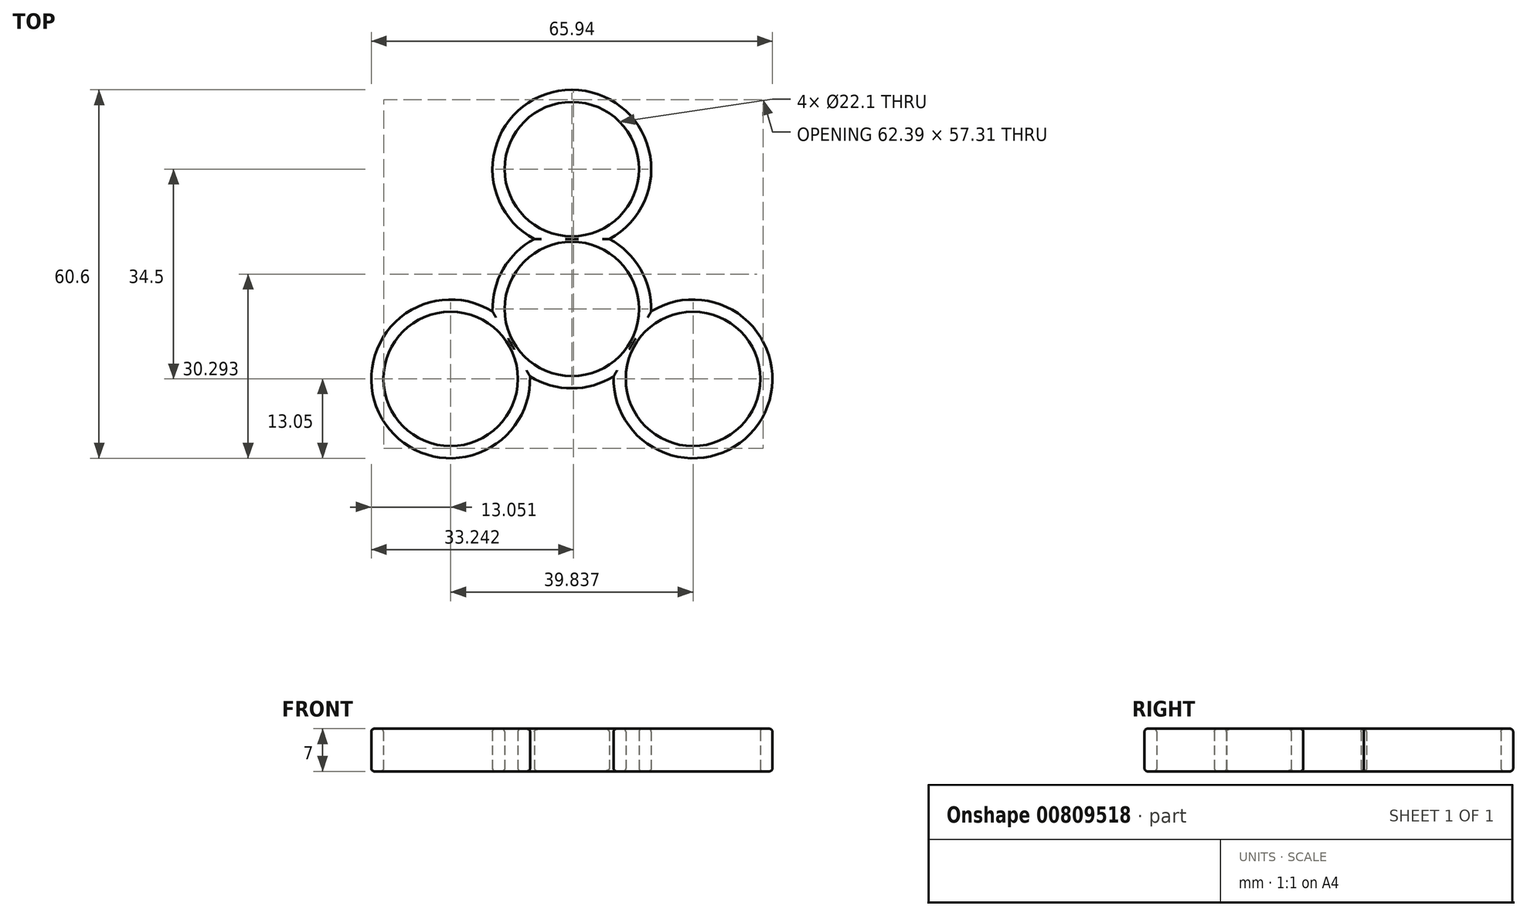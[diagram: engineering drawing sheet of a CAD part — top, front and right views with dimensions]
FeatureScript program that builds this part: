
annotation { "Feature Type Name" : "Feature", "Feature Type Description" : "" }
export const myFeature = defineFeature(function(context is Context, id is Id, definition is map)
    precondition{}
    {
        {
            var Q0;
            Q0=qCreatedBy(makeId("Top.planeOp"),FACE);
            var sketch = newSketch(context, id + "F0", { "sketchPlane" : qUnion([Q0])});
            skCircle(sketch, "E0", {"center": v(0, 0) * mm, "radius": 11.05 * mm});
            skCircle(sketch, "E1", {"center": v(0, 23) * mm, "radius": 11.05 * mm});
            skCircle(sketch, "E2", {"center": v(0, 23) * mm, "radius": 13.05 * mm});
            skCircle(sketch, "E3", {"center": v(0, 0) * mm, "radius": 13.05 * mm});
            skCircle(sketch, "E4.1.0", {"center": v(-19.92, -11.5) * mm, "radius": 11.05 * mm});
            skCircle(sketch, "E4.1.1", {"center": v(-19.92, -11.5) * mm, "radius": 13.05 * mm});
            skCircle(sketch, "E4.2.0", {"center": v(19.92, -11.5) * mm, "radius": 11.05 * mm});
            skCircle(sketch, "E4.2.1", {"center": v(19.92, -11.5) * mm, "radius": 13.05 * mm});
            skSolve(sketch);
        }
        {
            var Q0;
            {var subQ0=sQuery(id+"F0.wireOp",EDGE,"E3");var subQ1=sQuery(id+"F0.wireOp",EDGE,"E1");var subQ2=makeQuery(id+"F0.imprint","INTERSECT",VERTEX,{"disambiguationData":[OD(0.0)],"derivedFrom":[subQ1,subQ0]});Q0=makeQuery(id+"F0.imprint","IMPRINT",FACE,{"disambiguationData":[TD([[makeQuery(id+"F0.imprint","IMPRINT",EDGE,{"disambiguationData":[TD([[subQ2,1.0]])],"derivedFrom":subQ1}),-1.0]])]});}
            var Q1;
            {var subQ0=sQuery(id+"F0.wireOp",EDGE,"E1");var subQ1=sQuery(id+"F0.wireOp",EDGE,"E0");var subQ2=makeQuery(id+"F0.imprint","INTERSECT",VERTEX,{"derivedFrom":[subQ1,subQ0]});Q1=makeQuery(id+"F0.imprint","IMPRINT",FACE,{"disambiguationData":[TD([[makeQuery(id+"F0.imprint","IMPRINT",EDGE,{"disambiguationData":[TD([[subQ2,-1.0]])],"derivedFrom":subQ1}),-1.0]])]});}
            var Q2;
            {var subQ0=sQuery(id+"F0.wireOp",EDGE,"E2");var subQ1=sQuery(id+"F0.wireOp",EDGE,"E0");var subQ2=makeQuery(id+"F0.imprint","INTERSECT",VERTEX,{"disambiguationData":[OD(0.0)],"derivedFrom":[subQ1,subQ0]});Q2=makeQuery(id+"F0.imprint","IMPRINT",FACE,{"disambiguationData":[TD([[makeQuery(id+"F0.imprint","IMPRINT",EDGE,{"disambiguationData":[TD([[subQ2,1.0]])],"derivedFrom":subQ1}),-1.0]])]});}
            var Q3;
            {var subQ0=sQuery(id+"F0.wireOp",EDGE,"E1");var subQ1=sQuery(id+"F0.wireOp",EDGE,"E0");var subQ2=makeQuery(id+"F0.imprint","INTERSECT",VERTEX,{"derivedFrom":[subQ1,subQ0]});Q3=makeQuery(id+"F0.imprint","IMPRINT",FACE,{"disambiguationData":[TD([[makeQuery(id+"F0.imprint","IMPRINT",EDGE,{"disambiguationData":[TD([[subQ2,1.0]])],"derivedFrom":subQ1}),-1.0]])]});}
            var Q4;
            {var subQ0=sQuery(id+"F0.wireOp",EDGE,"E3");var subQ1=sQuery(id+"F0.wireOp",EDGE,"E1");var subQ2=makeQuery(id+"F0.imprint","INTERSECT",VERTEX,{"disambiguationData":[OD(0.0)],"derivedFrom":[subQ1,subQ0]});Q4=makeQuery(id+"F0.imprint","IMPRINT",FACE,{"disambiguationData":[TD([[makeQuery(id+"F0.imprint","IMPRINT",EDGE,{"disambiguationData":[TD([[subQ2,-1.0]])],"derivedFrom":subQ1}),-1.0]])]});}
            var Q5;
            {var subQ4=sQuery(id+"F0.wireOp",EDGE,"E4.1.1");var subQ5=sQuery(id+"F0.wireOp",EDGE,"E0");var subQ6=makeQuery(id+"F0.imprint","INTERSECT",VERTEX,{"disambiguationData":[OD(0.0)],"derivedFrom":[subQ5,subQ4]});Q5=makeQuery(id+"F0.imprint","IMPRINT",FACE,{"disambiguationData":[TD([[makeQuery(id+"F0.imprint","IMPRINT",EDGE,{"disambiguationData":[TD([[subQ6,-1.0]])],"derivedFrom":subQ5}),-1.0]])]});}
            var Q6;
            {var subQ0=sQuery(id+"F0.wireOp",EDGE,"E4.1.1");var subQ1=sQuery(id+"F0.wireOp",EDGE,"E3");var subQ2=makeQuery(id+"F0.imprint","INTERSECT",VERTEX,{"disambiguationData":[OD(0.0)],"derivedFrom":[subQ1,subQ0]});Q6=makeQuery(id+"F0.imprint","IMPRINT",FACE,{"disambiguationData":[TD([[makeQuery(id+"F0.imprint","IMPRINT",EDGE,{"disambiguationData":[TD([[subQ2,-1.0]])],"derivedFrom":subQ1}),-1.0]])]});}
            var Q7;
            {var subQ0=sQuery(id+"F0.wireOp",EDGE,"E4.2.1");var subQ1=sQuery(id+"F0.wireOp",EDGE,"E3");var subQ2=makeQuery(id+"F0.imprint","INTERSECT",VERTEX,{"disambiguationData":[OD(0.0)],"derivedFrom":[subQ1,subQ0]});Q7=makeQuery(id+"F0.imprint","IMPRINT",FACE,{"disambiguationData":[TD([[makeQuery(id+"F0.imprint","IMPRINT",EDGE,{"disambiguationData":[TD([[subQ2,-1.0]])],"derivedFrom":subQ1}),-1.0]])]});}
            var Q8;
            {var subQ0=sQuery(id+"F0.wireOp",EDGE,"E4.2.1");var subQ7=sQuery(id+"F0.wireOp",EDGE,"E0");var subQ8=makeQuery(id+"F0.imprint","INTERSECT",VERTEX,{"disambiguationData":[OD(0.0)],"derivedFrom":[subQ7,subQ0]});Q8=makeQuery(id+"F0.imprint","IMPRINT",FACE,{"disambiguationData":[TD([[makeQuery(id+"F0.imprint","IMPRINT",EDGE,{"disambiguationData":[TD([[subQ8,-1.0]])],"derivedFrom":subQ7}),-1.0]])]});}
            extrude(context, id + "F1", {"entities" : qUnion([Q0, Q1, Q2, Q3, Q4, Q5, Q6, Q7, Q8]), "depth" : 7 * mm, "offsetDistance" : 25 * mm});
        }
        {
            var Q0;
            Q0=makeQuery(id+"F1.opExtrude","CAP_FACE",FACE,{"disambiguationData":[OSD([sQuery(id+"F0.wireOp",EDGE,"E0"),sQuery(id+"F0.wireOp",EDGE,"E1"),sQuery(id+"F0.wireOp",EDGE,"E2"),sQuery(id+"F0.wireOp",EDGE,"E3"),sQuery(id+"F0.wireOp",EDGE,"E4.1.0"),sQuery(id+"F0.wireOp",EDGE,"E4.1.1"),sQuery(id+"F0.wireOp",EDGE,"E4.2.0"),sQuery(id+"F0.wireOp",EDGE,"E4.2.1")])],"isStart":false});
            var Q1;
            Q1=makeQuery(id+"F1.opExtrude","CAP_FACE",FACE,{"disambiguationData":[OSD([sQuery(id+"F0.wireOp",EDGE,"E0"),sQuery(id+"F0.wireOp",EDGE,"E1"),sQuery(id+"F0.wireOp",EDGE,"E2"),sQuery(id+"F0.wireOp",EDGE,"E3"),sQuery(id+"F0.wireOp",EDGE,"E4.1.0"),sQuery(id+"F0.wireOp",EDGE,"E4.1.1"),sQuery(id+"F0.wireOp",EDGE,"E4.2.0"),sQuery(id+"F0.wireOp",EDGE,"E4.2.1")])],"isStart":true});
            fillet(context, id + "F2", {"entities" : qUnion([Q0, Q1]), "radius" : .5 * mm, "tangentPropagation" : true, "allowEdgeOverflow" : false});
        }
    });
